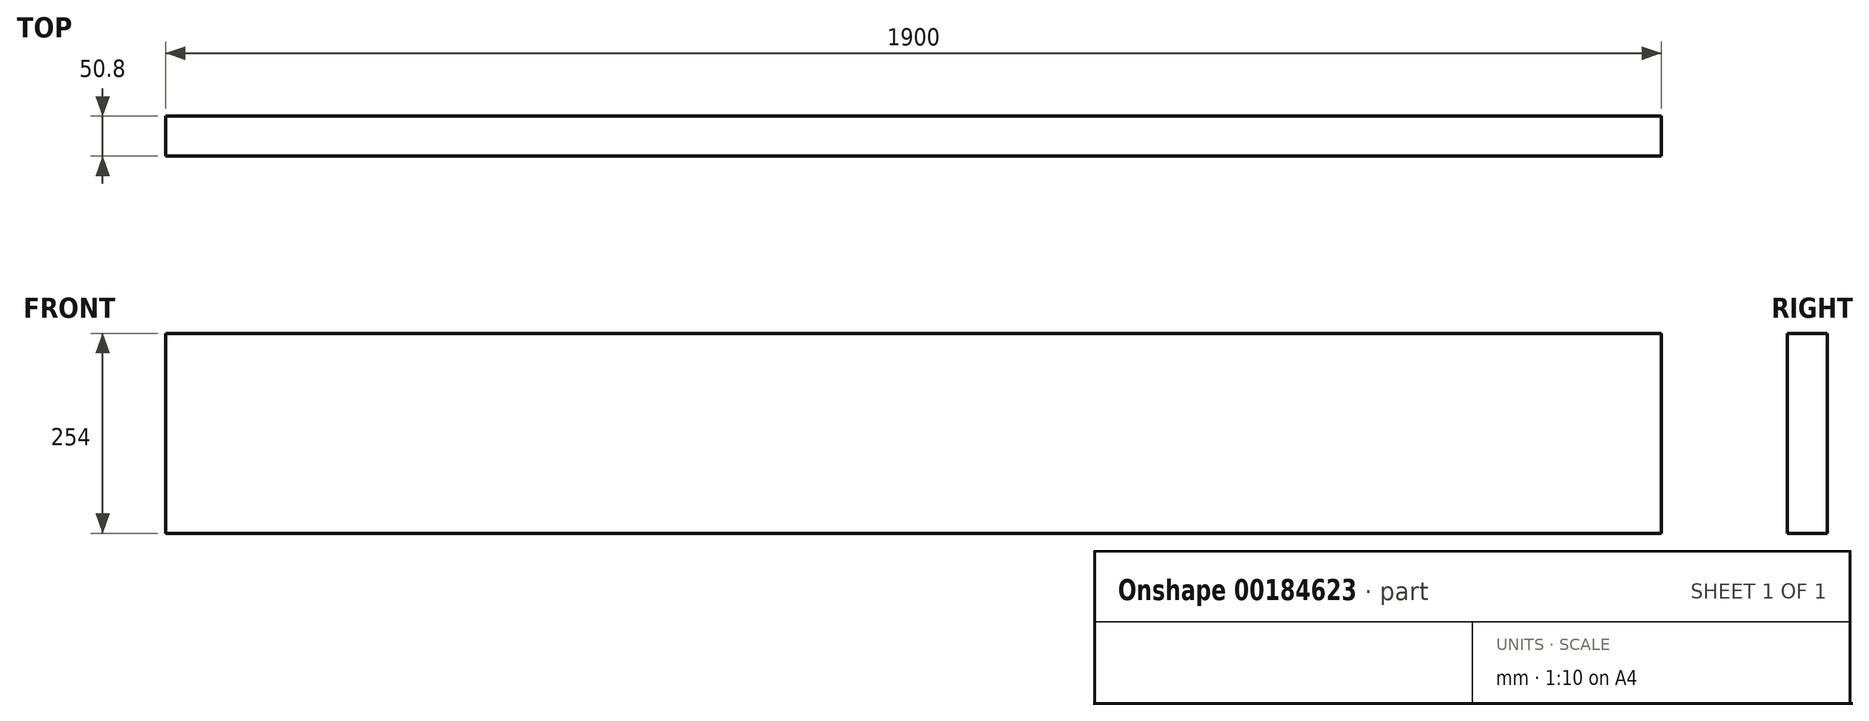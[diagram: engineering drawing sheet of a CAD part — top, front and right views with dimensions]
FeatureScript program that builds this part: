
annotation { "Feature Type Name" : "Feature", "Feature Type Description" : "" }
export const myFeature = defineFeature(function(context is Context, id is Id, definition is map)
    precondition{}
    {
        {
            var Q0;
            Q0=qCreatedBy(makeId("Front.planeOp"),FACE);
            var sketch = newSketch(context, id + "F0", { "sketchPlane" : qUnion([Q0])});
            skLineSegment(sketch, "E0.bottom", {"start": v(950, -127) * mm, "end": v(-950, -127) * mm});
            skLineSegment(sketch, "E0.top", {"start": v(950, 127) * mm, "end": v(-950, 127) * mm});
            skLineSegment(sketch, "E0.left", {"start": v(950, -127) * mm, "end": v(950, 127) * mm});
            skLineSegment(sketch, "E0.right", {"start": v(-950, -127) * mm, "end": v(-950, 127) * mm});
            skPoint(sketch, "E0.middle", {"position": v(0, 0) * mm});
            skSolve(sketch);
        }
        {
            var Q0;
            Q0 = qSketchRegion(id + "F0", true);
            extrude(context, id + "F1", {"entities" : qUnion([Q0]), "endBound" : BoundingType.SYMMETRIC, "depth" : 50.8 * mm});
        }
    });
